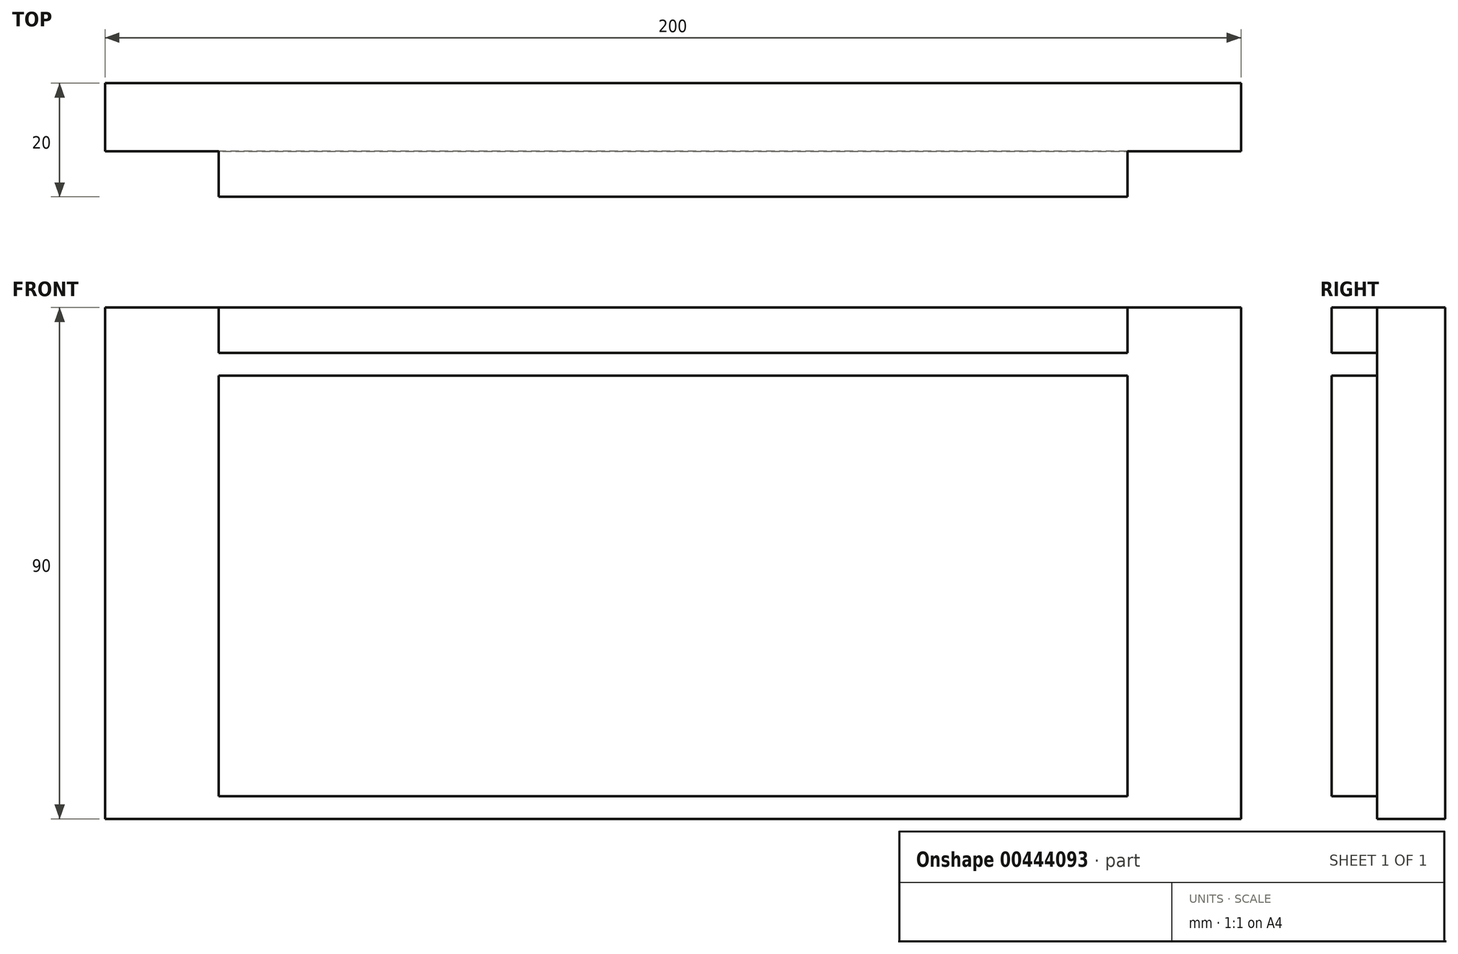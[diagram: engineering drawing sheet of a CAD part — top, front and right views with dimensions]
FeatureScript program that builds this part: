
annotation { "Feature Type Name" : "Feature", "Feature Type Description" : "" }
export const myFeature = defineFeature(function(context is Context, id is Id, definition is map)
    precondition{}
    {
        {
            var Q0;
            Q0=qCreatedBy(makeId("Front.planeOp"),FACE);
            var sketch = newSketch(context, id + "F0", { "sketchPlane" : qUnion([Q0])});
            skLineSegment(sketch, "E0.bottom", {"start": v(-100, 45) * mm, "end": v(100, 45) * mm});
            skLineSegment(sketch, "E0.top", {"start": v(-100, -45) * mm, "end": v(100, -45) * mm});
            skLineSegment(sketch, "E0.left", {"start": v(-100, 45) * mm, "end": v(-100, -45) * mm});
            skLineSegment(sketch, "E0.right", {"start": v(100, 45) * mm, "end": v(100, -45) * mm});
            skPoint(sketch, "E0.middle", {"position": v(0, 0) * mm});
            skLineSegment(sketch, "E1", {"start": v(-80, 45) * mm, "end": v(-80, -45) * mm});
            skLineSegment(sketch, "E2", {"start": v(80, 45) * mm, "end": v(80, -45) * mm});
            skLineSegment(sketch, "E3", {"start": v(80, 37) * mm, "end": v(-80, 37) * mm});
            skLineSegment(sketch, "E4", {"start": v(-80, 33) * mm, "end": v(80, 33) * mm});
            skLineSegment(sketch, "E5", {"start": v(80, -41) * mm, "end": v(-80, -41) * mm});
            skSolve(sketch);
        }
        {
            var Q0;
            {var subQ0=sQuery(id+"F0.wireOp",EDGE,"E0.left");Q0=makeQuery(id+"F0.imprint","IMPRINT",FACE,{"disambiguationData":[TD([[makeQuery(id+"F0.imprint","IMPRINT",EDGE,{"derivedFrom":subQ0}),1.0]])]});}
            var Q1;
            {var subQ0=sQuery(id+"F0.wireOp",EDGE,"E0.right");Q1=makeQuery(id+"F0.imprint","IMPRINT",FACE,{"disambiguationData":[TD([[makeQuery(id+"F0.imprint","IMPRINT",EDGE,{"derivedFrom":subQ0}),-1.0]])]});}
            var Q2;
            {var subQ5=sQuery(id+"F0.wireOp",EDGE,"E5");Q2=makeQuery(id+"F0.imprint","IMPRINT",FACE,{"disambiguationData":[TD([[makeQuery(id+"F0.imprint","IMPRINT",EDGE,{"derivedFrom":subQ5}),1.0]])]});}
            var Q3;
            {var subQ0=sQuery(id+"F0.wireOp",EDGE,"E3");Q3=makeQuery(id+"F0.imprint","IMPRINT",FACE,{"disambiguationData":[TD([[makeQuery(id+"F0.imprint","IMPRINT",EDGE,{"derivedFrom":subQ0}),1.0]])]});}
            extrude(context, id + "F1", {"entities" : qUnion([Q0, Q1, Q2, Q3]), "depth" : 12 * mm});
        }
        {
            var Q0;
            {var subQ0=sQuery(id+"F0.wireOp",EDGE,"E4");Q0=makeQuery(id+"F0.imprint","IMPRINT",FACE,{"disambiguationData":[TD([[makeQuery(id+"F0.imprint","IMPRINT",EDGE,{"derivedFrom":subQ0}),-1.0]])]});}
            var Q1;
            {var subQ5=sQuery(id+"F0.wireOp",EDGE,"E3");Q1=makeQuery(id+"F0.imprint","IMPRINT",FACE,{"disambiguationData":[TD([[makeQuery(id+"F0.imprint","IMPRINT",EDGE,{"derivedFrom":subQ5}),-1.0]])]});}
            extrude(context, id + "F2", {"entities" : qUnion([Q0, Q1]), "operationType" : NewBodyOperationType.ADD, "depth" : 20 * mm});
        }
    });
